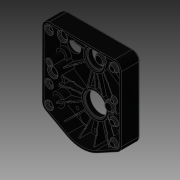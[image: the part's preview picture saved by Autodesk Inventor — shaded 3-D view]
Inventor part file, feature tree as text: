
AUTODESK INVENTOR PART (.ipt)
format: ipt  version: 2014 SP1 (Build 180222100, 222)  size: 1,041,408 bytes
history: native  units: in
note: dims shown in document units (in); Inventor stores cm internally (conversion verified against a paired STEP export)
features: fillet x1, other x1, imported_body x1
ambient origin geometry x8: Origin, YZ Plane, XZ Plane, XY Plane, X Axis, Y Axis, Z Axis, Center Point
bodies: Body1 (feature_tree)
feature tree (3):
  fillet  "Fillet18"  [1 undecoded]
  other  "217-2428-001 Rev1.ipt1"
  imported_body  "Base1"
note: 1 required parameter value undecoded (feature->parameter linkage not recoverable at this tier; creation-order binding heuristic only, values carry confidence <= 0.55)
